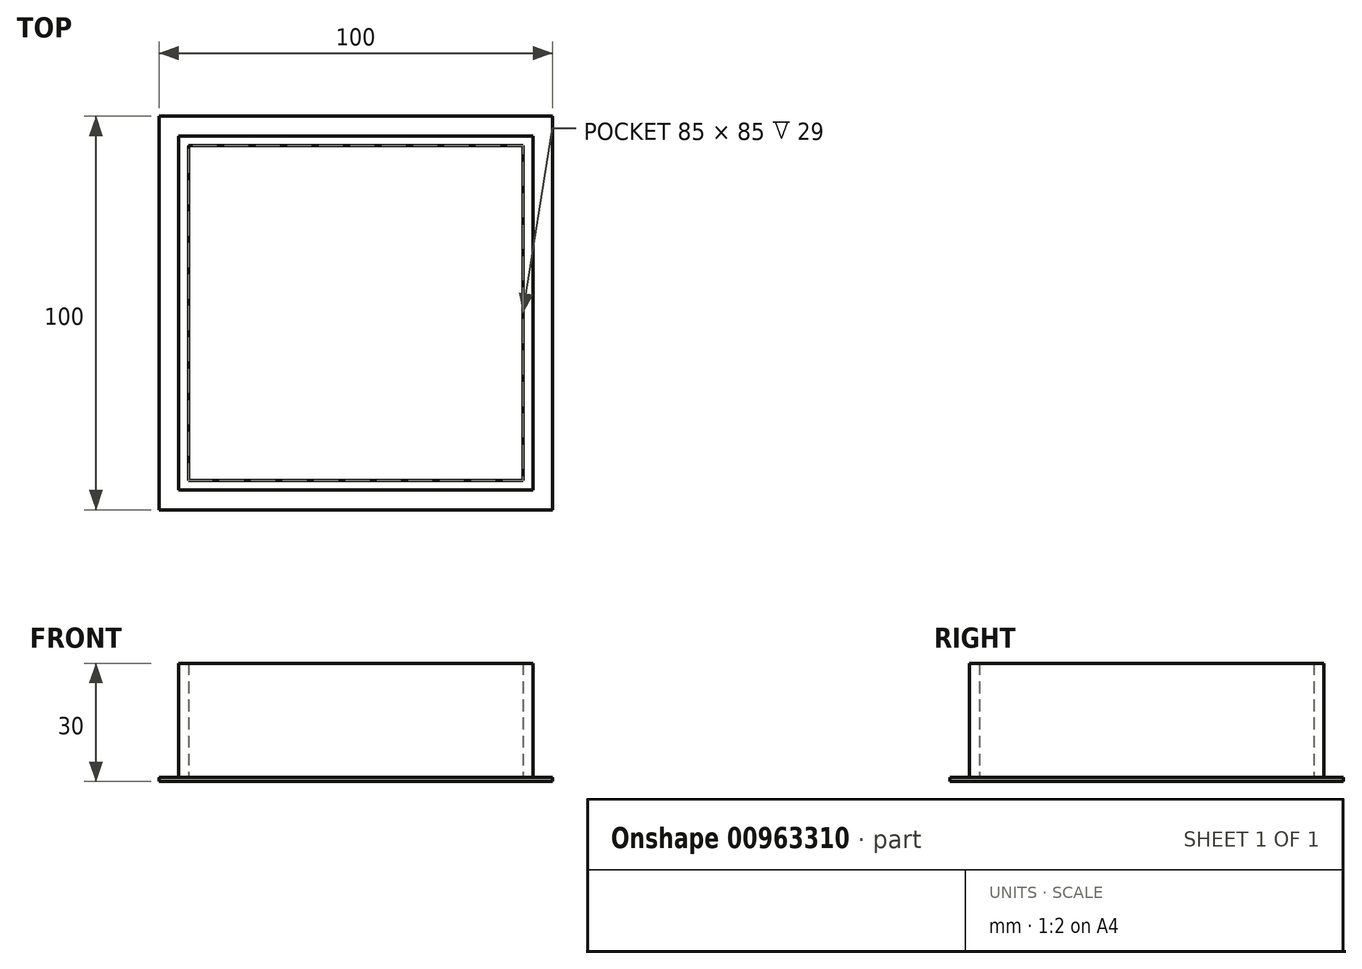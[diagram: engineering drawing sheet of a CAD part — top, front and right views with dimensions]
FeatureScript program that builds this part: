
annotation { "Feature Type Name" : "Feature", "Feature Type Description" : "" }
export const myFeature = defineFeature(function(context is Context, id is Id, definition is map)
    precondition{}
    {
        {
            var Q0;
            Q0=qCreatedBy(makeId("Top.planeOp"),FACE);
            var sketch = newSketch(context, id + "F0", { "sketchPlane" : qUnion([Q0])});
            skLineSegment(sketch, "E0.bottom", {"start": v(50, 50) * mm, "end": v(-50, 50) * mm});
            skLineSegment(sketch, "E0.top", {"start": v(50, -50) * mm, "end": v(-50, -50) * mm});
            skLineSegment(sketch, "E0.left", {"start": v(50, 50) * mm, "end": v(50, -50) * mm});
            skLineSegment(sketch, "E0.right", {"start": v(-50, 50) * mm, "end": v(-50, -50) * mm});
            skPoint(sketch, "E0.middle", {"position": v(0, 0) * mm});
            skLineSegment(sketch, "E1.bottom", {"start": v(45, -45) * mm, "end": v(-45, -45) * mm});
            skLineSegment(sketch, "E1.top", {"start": v(45, 45) * mm, "end": v(-45, 45) * mm});
            skLineSegment(sketch, "E1.left", {"start": v(45, -45) * mm, "end": v(45, 45) * mm});
            skLineSegment(sketch, "E1.right", {"start": v(-45, -45) * mm, "end": v(-45, 45) * mm});
            skLineSegment(sketch, "E2.bottom", {"start": v(-42.5, 42.5) * mm, "end": v(42.5, 42.5) * mm});
            skLineSegment(sketch, "E2.top", {"start": v(-42.5, -42.5) * mm, "end": v(42.5, -42.5) * mm});
            skLineSegment(sketch, "E2.left", {"start": v(-42.5, 42.5) * mm, "end": v(-42.5, -42.5) * mm});
            skLineSegment(sketch, "E2.right", {"start": v(42.5, 42.5) * mm, "end": v(42.5, -42.5) * mm});
            skSolve(sketch);
        }
        {
            var Q0;
            Q0=makeQuery(id+"F0.imprint","IMPRINT",FACE,{"disambiguationData":[TD([[makeQuery(id+"F0.imprint","IMPRINT",EDGE,{"derivedFrom":sQuery(id+"F0.wireOp",EDGE,"E1.bottom")}),-1.0]])]});
            extrude(context, id + "F1", {"entities" : qUnion([Q0]), "depth" : 30 * mm, "offsetDistance" : 25.4 * mm});
        }
        {
            var Q0;
            Q0=makeQuery(id+"F0.imprint","IMPRINT",FACE,{"disambiguationData":[TD([[makeQuery(id+"F0.imprint","IMPRINT",EDGE,{"derivedFrom":sQuery(id+"F0.wireOp",EDGE,"E0.bottom")}),1.0]])]});
            var Q1;
            Q1=makeQuery(id+"F0.imprint","IMPRINT",FACE,{"disambiguationData":[TD([[makeQuery(id+"F0.imprint","IMPRINT",EDGE,{"derivedFrom":sQuery(id+"F0.wireOp",EDGE,"E2.bottom")}),-1.0]])]});
            extrude(context, id + "F2", {"entities" : qUnion([Q0, Q1]), "operationType" : NewBodyOperationType.ADD, "depth" : 1 * mm, "offsetDistance" : 25.4 * mm});
        }
    });
